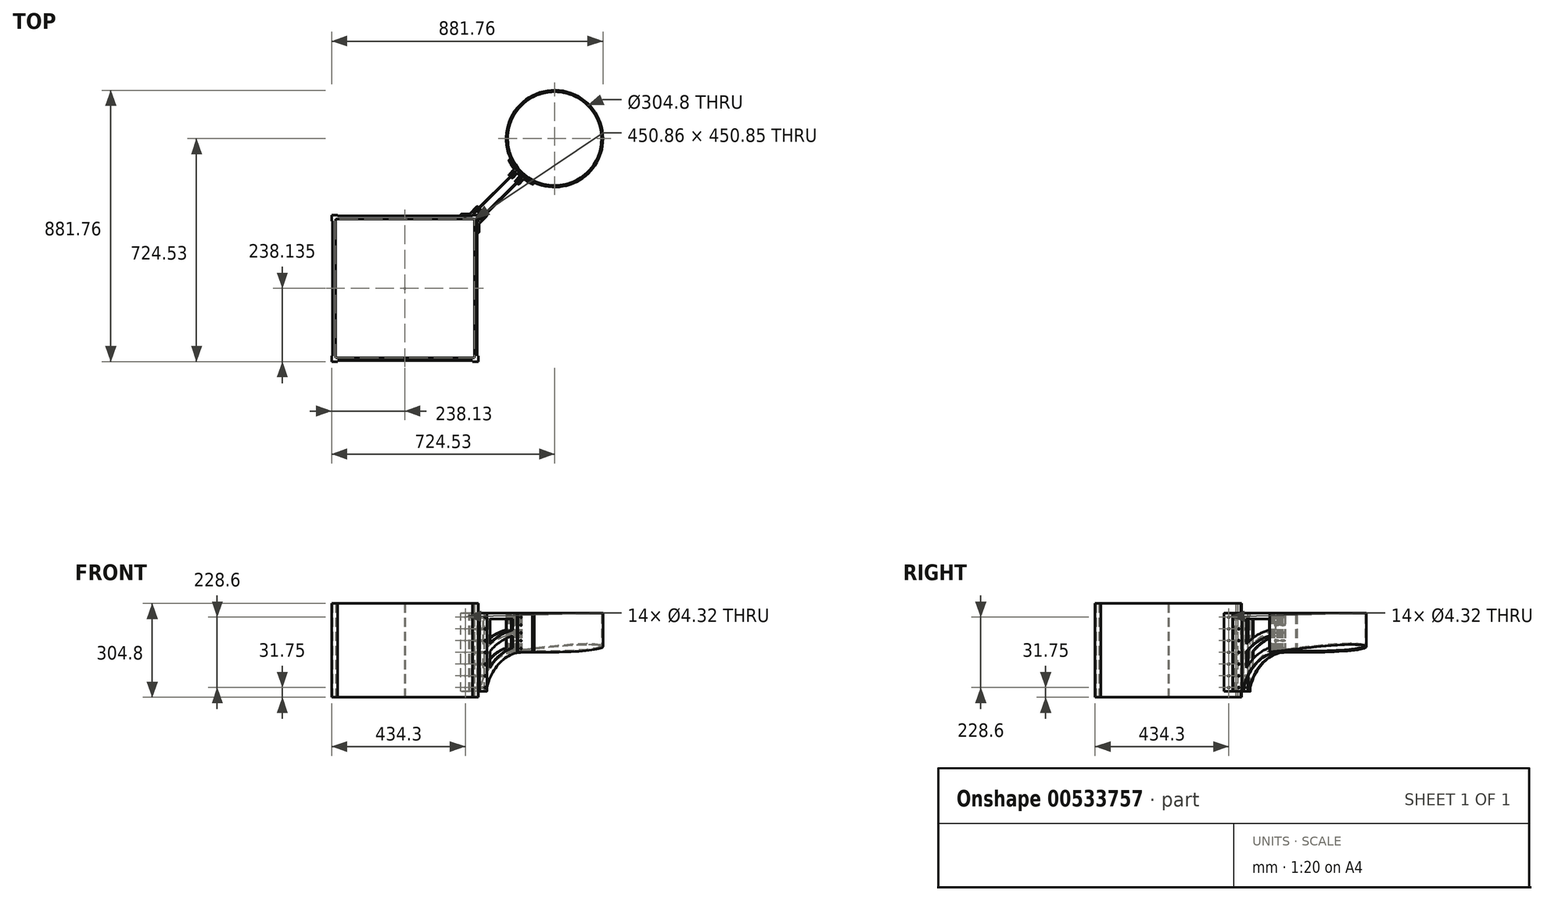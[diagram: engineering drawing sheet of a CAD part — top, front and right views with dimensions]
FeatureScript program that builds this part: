
annotation { "Feature Type Name" : "Feature", "Feature Type Description" : "" }
export const myFeature = defineFeature(function(context is Context, id is Id, definition is map)
    precondition{}
    {
        {
            var Q0;
            Q0=qCreatedBy(makeId("Top.planeOp"),FACE);
            var sketch = newSketch(context, id + "F0", { "sketchPlane" : qUnion([Q0])});
            skLineSegment(sketch, "E0.bottom", {"start": v(234.95, -234.95) * mm, "end": v(-234.95, -234.95) * mm});
            skLineSegment(sketch, "E0.top", {"start": v(234.95, 234.95) * mm, "end": v(-234.95, 234.95) * mm});
            skLineSegment(sketch, "E0.left", {"start": v(234.95, -234.95) * mm, "end": v(234.95, 234.95) * mm});
            skLineSegment(sketch, "E0.right", {"start": v(-234.95, -234.95) * mm, "end": v(-234.95, 234.95) * mm});
            skPoint(sketch, "E0.middle", {"position": v(0, 0) * mm});
            skLineSegment(sketch, "E1", {"start": v(0, 0) * mm, "end": v(234.95, 234.95) * mm});
            skLineSegment(sketch, "E2", {"start": v(234.95, 234.95) * mm, "end": v(486.4, 486.4) * mm});
            skCircle(sketch, "E3", {"center": v(486.4, 486.4) * mm, "radius": 152.4 * mm});
            skCircle(sketch, "E4", {"center": v(486.4, 486.4) * mm, "radius": 157.23 * mm});
            skLineSegment(sketch, "E5", {"start": v(-234.95, 234.95) * mm, "end": v(-234.95, 238.13) * mm});
            skLineSegment(sketch, "E6", {"start": v(-234.95, 238.13) * mm, "end": v(-238.13, 238.13) * mm});
            skLineSegment(sketch, "E7", {"start": v(-238.13, 238.13) * mm, "end": v(-238.13, 219.08) * mm});
            skLineSegment(sketch, "E8", {"start": v(-238.13, 219.08) * mm, "end": v(-234.95, 219.08) * mm});
            skLineSegment(sketch, "E9", {"start": v(-238.13, 238.13) * mm, "end": v(-219.08, 238.13) * mm});
            skLineSegment(sketch, "E10", {"start": v(-219.08, 238.13) * mm, "end": v(-219.08, 234.95) * mm});
            skLineSegment(sketch, "E11.1.0", {"start": v(-238.13, -238.13) * mm, "end": v(-219.08, -238.13) * mm});
            skLineSegment(sketch, "E11.1.1", {"start": v(-238.13, -238.13) * mm, "end": v(-238.13, -219.08) * mm});
            skLineSegment(sketch, "E11.1.2", {"start": v(-238.13, -219.08) * mm, "end": v(-234.95, -219.08) * mm});
            skLineSegment(sketch, "E11.1.3", {"start": v(-219.08, -238.13) * mm, "end": v(-219.08, -234.95) * mm});
            skLineSegment(sketch, "E11.1.4", {"start": v(-238.13, -234.95) * mm, "end": v(-238.13, -238.13) * mm});
            skLineSegment(sketch, "E11.1.5", {"start": v(-234.95, -234.95) * mm, "end": v(-238.13, -234.95) * mm});
            skLineSegment(sketch, "E11.2.0", {"start": v(238.13, -238.13) * mm, "end": v(238.13, -219.08) * mm});
            skLineSegment(sketch, "E11.2.1", {"start": v(238.13, -238.13) * mm, "end": v(219.08, -238.13) * mm});
            skLineSegment(sketch, "E11.2.2", {"start": v(219.08, -238.13) * mm, "end": v(219.08, -234.95) * mm});
            skLineSegment(sketch, "E11.2.3", {"start": v(238.13, -219.08) * mm, "end": v(234.95, -219.08) * mm});
            skLineSegment(sketch, "E11.2.4", {"start": v(234.95, -238.13) * mm, "end": v(238.13, -238.13) * mm});
            skLineSegment(sketch, "E11.2.5", {"start": v(234.95, -234.95) * mm, "end": v(234.95, -238.13) * mm});
            skLineSegment(sketch, "E11.3.0", {"start": v(238.13, 238.13) * mm, "end": v(219.08, 238.13) * mm});
            skLineSegment(sketch, "E11.3.1", {"start": v(238.13, 238.13) * mm, "end": v(238.13, 219.08) * mm});
            skLineSegment(sketch, "E11.3.2", {"start": v(238.13, 219.08) * mm, "end": v(234.95, 219.08) * mm});
            skLineSegment(sketch, "E11.3.3", {"start": v(219.08, 238.13) * mm, "end": v(219.08, 234.95) * mm});
            skLineSegment(sketch, "E11.3.4", {"start": v(238.13, 234.95) * mm, "end": v(238.13, 238.13) * mm});
            skLineSegment(sketch, "E11.3.5", {"start": v(234.95, 234.95) * mm, "end": v(238.13, 234.95) * mm});
            skLineSegment(sketch, "E12.0", {"start": v(-225.42, -225.42) * mm, "end": v(-225.43, 225.43) * mm});
            skLineSegment(sketch, "E12.1", {"start": v(225.43, -225.42) * mm, "end": v(-225.42, -225.42) * mm});
            skLineSegment(sketch, "E12.2", {"start": v(225.43, -225.42) * mm, "end": v(225.42, 225.43) * mm});
            skLineSegment(sketch, "E12.3", {"start": v(225.42, 225.43) * mm, "end": v(-225.43, 225.43) * mm});
            skSolve(sketch);
        }
        {
            var Q0;
            Q0=makeQuery(id+"F0.imprint","IMPRINT",FACE,{"disambiguationData":[TD([[makeQuery(id+"F0.imprint","IMPRINT",EDGE,{"derivedFrom":sQuery(id+"F0.wireOp",EDGE,"E3")}),-1.0]])]});
            extrude(context, id + "F1", {"entities" : qUnion([Q0]), "depth" : 304.8 * mm, "offsetDistance" : 25.4 * mm});
        }
        {
            var Q0;
            Q0=makeQuery(id+"F0.imprint","IMPRINT",FACE,{"disambiguationData":[TD([[makeQuery(id+"F0.imprint","IMPRINT",EDGE,{"derivedFrom":sQuery(id+"F0.wireOp",EDGE,"E12.0")}),1.0]])]});
            var Q1;
            Q1=makeQuery(id+"F0.imprint","IMPRINT",FACE,{"disambiguationData":[TD([[makeQuery(id+"F0.imprint","IMPRINT",EDGE,{"derivedFrom":sQuery(id+"F0.wireOp",EDGE,"E11.3.1")}),-1.0]])]});
            var Q2;
            {var subQ4=sQuery(id+"F0.wireOp",EDGE,"E11.3.0");Q2=makeQuery(id+"F0.imprint","IMPRINT",FACE,{"disambiguationData":[TD([[makeQuery(id+"F0.imprint","IMPRINT",EDGE,{"derivedFrom":subQ4}),1.0]])]});}
            var Q3;
            Q3=makeQuery(id+"F0.imprint","IMPRINT",FACE,{"disambiguationData":[TD([[makeQuery(id+"F0.imprint","IMPRINT",EDGE,{"derivedFrom":sQuery(id+"F0.wireOp",EDGE,"E11.2.0")}),1.0]])]});
            var Q4;
            {var subQ1=sQuery(id+"F0.wireOp",EDGE,"E5");Q4=makeQuery(id+"F0.imprint","IMPRINT",FACE,{"disambiguationData":[TD([[makeQuery(id+"F0.imprint","IMPRINT",EDGE,{"derivedFrom":subQ1}),1.0]])]});}
            var Q5;
            Q5=makeQuery(id+"F0.imprint","IMPRINT",FACE,{"disambiguationData":[TD([[makeQuery(id+"F0.imprint","IMPRINT",EDGE,{"derivedFrom":sQuery(id+"F0.wireOp",EDGE,"E11.2.1")}),-1.0]])]});
            var Q6;
            {var subQ0=sQuery(id+"F0.wireOp",EDGE,"E5");Q6=makeQuery(id+"F0.imprint","IMPRINT",FACE,{"disambiguationData":[TD([[makeQuery(id+"F0.imprint","IMPRINT",EDGE,{"derivedFrom":subQ0}),-1.0]])]});}
            var Q7;
            Q7=makeQuery(id+"F0.imprint","IMPRINT",FACE,{"disambiguationData":[TD([[makeQuery(id+"F0.imprint","IMPRINT",EDGE,{"derivedFrom":sQuery(id+"F0.wireOp",EDGE,"E11.1.0")}),1.0]])]});
            var Q8;
            Q8=makeQuery(id+"F0.imprint","IMPRINT",FACE,{"disambiguationData":[TD([[makeQuery(id+"F0.imprint","IMPRINT",EDGE,{"derivedFrom":sQuery(id+"F0.wireOp",EDGE,"E11.1.1")}),-1.0]])]});
            var Q9;
            {var subQ2=sQuery(id+"F0.wireOp",EDGE,"E11.3.4");Q9=makeQuery(id+"F0.imprint","IMPRINT",FACE,{"disambiguationData":[TD([[makeQuery(id+"F0.imprint","IMPRINT",EDGE,{"derivedFrom":subQ2}),1.0]])]});}
            extrude(context, id + "F2", {"entities" : qUnion([Q0, Q1, Q2, Q3, Q4, Q5, Q6, Q7, Q8, Q9]), "depth" : 304.8 * mm, "offsetDistance" : 25.4 * mm});
        }
        {
            var Q0;
            Q0=makeQuery(id+"F1.opExtrude","CAP_FACE",FACE,{"disambiguationData":[OSD([sQuery(id+"F0.wireOp",EDGE,"E3"),sQuery(id+"F0.wireOp",EDGE,"E4")])],"isStart":false});
            var sketch = newSketch(context, id + "F3", { "sketchPlane" : qUnion([Q0])});
            skCircle(sketch, "E13", {"center": v(486.4, 486.4) * mm, "radius": 157.23 * mm});
            skArc(sketch, "E14", {"start": v(366.99, 372.3) * mm, "mid": v(369.6, 369.6) * mm, "end": v(372.3, 366.99) * mm});
            skLineSegment(sketch, "E15", {"start": v(486.4, 486.4) * mm, "end": v(643.62, 486.4) * mm});
            skLineSegment(sketch, "E16", {"start": v(643.62, 486.4) * mm, "end": v(645.21, 486.4) * mm});
            skCircle(sketch, "E17", {"center": v(486.4, 486.4) * mm, "radius": 158.81 * mm});
            skLineSegment(sketch, "E18", {"start": v(369.6, 369.6) * mm, "end": v(244.47, 244.48) * mm});
            skLineSegment(sketch, "E19", {"start": v(486.4, 486.4) * mm, "end": v(477.42, 495.38) * mm});
            skLineSegment(sketch, "E20", {"start": v(360.97, 378.93) * mm, "end": v(345.53, 363.49) * mm});
            skLineSegment(sketch, "E21", {"start": v(477.42, 495.38) * mm, "end": v(475.17, 497.62) * mm});
            skLineSegment(sketch, "E22", {"start": v(358.92, 381.37) * mm, "end": v(343.28, 365.73) * mm});
            skLineSegment(sketch, "E23", {"start": v(645.21, 486.4) * mm, "end": v(651.56, 486.4) * mm});
            skLineSegment(sketch, "E24", {"start": v(238.13, 238.13) * mm, "end": v(219.08, 238.13) * mm});
            skLineSegment(sketch, "E25", {"start": v(219.08, 238.13) * mm, "end": v(219.08, 234.95) * mm});
            skLineSegment(sketch, "E26", {"start": v(219.08, 234.95) * mm, "end": v(180.98, 234.95) * mm});
            skLineSegment(sketch, "E27", {"start": v(180.98, 234.95) * mm, "end": v(180.98, 238.76) * mm});
            skLineSegment(sketch, "E28", {"start": v(475.17, 497.62) * mm, "end": v(470.68, 502.11) * mm});
            skLineSegment(sketch, "E29", {"start": v(353.4, 384.83) * mm, "end": v(338.8, 370.22) * mm});
            skLineSegment(sketch, "E30", {"start": v(477.42, 495.38) * mm, "end": v(481.9, 490.89) * mm});
            skLineSegment(sketch, "E31", {"start": v(363.35, 372.33) * mm, "end": v(350.02, 359) * mm});
            skLineSegment(sketch, "E32", {"start": v(353.4, 384.83) * mm, "end": v(337, 368.43) * mm});
            skLineSegment(sketch, "E33", {"start": v(338.8, 366.63) * mm, "end": v(339.69, 365.73) * mm});
            skArc(sketch, "E34.trimOffspring", {"start": v(358.92, 381.37) * mm, "mid": v(359.94, 380.15) * mm, "end": v(360.97, 378.93) * mm});
            skLineSegment(sketch, "E35.trimOffspring", {"start": v(345.53, 359.9) * mm, "end": v(346.42, 359) * mm});
            skLineSegment(sketch, "E36", {"start": v(235.5, 244.48) * mm, "end": v(245.3, 254.29) * mm});
            skLineSegment(sketch, "E37", {"start": v(245.3, 257.88) * mm, "end": v(244.41, 258.78) * mm});
            skLineSegment(sketch, "E38.trimOffspring", {"start": v(234.08, 265.51) * mm, "end": v(210.61, 242.04) * mm});
            skLineSegment(sketch, "E39.trimOffspring", {"start": v(247.1, 256.09) * mm, "end": v(235.5, 244.47) * mm});
            skLineSegment(sketch, "E40", {"start": v(183.52, 241.3) * mm, "end": v(208.82, 241.3) * mm});
            skLineSegment(sketch, "E41", {"start": v(238.13, 244.48) * mm, "end": v(235.5, 244.48) * mm});
            skLineSegment(sketch, "E42", {"start": v(223.34, 241.3) * mm, "end": v(221.1, 243.55) * mm});
            skLineSegment(sketch, "E43.trimOffspring", {"start": v(238.57, 264.62) * mm, "end": v(237.68, 265.51) * mm});
            skLineSegment(sketch, "E44", {"start": v(486.4, 486.4) * mm, "end": v(339.03, 417.68) * mm});
            skPoint(sketch, "E45.visualSharp", {"position": v(354.96, 386.39) * mm});
            skArc(sketch, "E45.filletArc", {"start": v(353.4, 384.83) * mm, "mid": v(354.13, 386.44) * mm, "end": v(353.64, 388.14) * mm});
            skPoint(sketch, "E46.visualSharp", {"position": v(337, 368.43) * mm});
            skArc(sketch, "E46.filletArc", {"start": v(338.8, 370.22) * mm, "mid": v(338.05, 368.43) * mm, "end": v(338.8, 366.63) * mm});
            skPoint(sketch, "E47.visualSharp", {"position": v(348.22, 357.2) * mm});
            skArc(sketch, "E47.filletArc", {"start": v(346.42, 359) * mm, "mid": v(348.22, 358.25) * mm, "end": v(350.02, 359) * mm});
            skPoint(sketch, "E48.visualSharp", {"position": v(365.2, 374.19) * mm});
            skArc(sketch, "E48.filletArc", {"start": v(366.99, 372.3) * mm, "mid": v(365.18, 373.08) * mm, "end": v(363.35, 372.33) * mm});
            skPoint(sketch, "E49.visualSharp", {"position": v(235.88, 267.31) * mm});
            skArc(sketch, "E49.filletArc", {"start": v(237.68, 265.51) * mm, "mid": v(235.88, 266.26) * mm, "end": v(234.08, 265.51) * mm});
            skPoint(sketch, "E50.visualSharp", {"position": v(247.1, 256.09) * mm});
            skArc(sketch, "E50.filletArc", {"start": v(245.3, 254.29) * mm, "mid": v(246.05, 256.09) * mm, "end": v(245.3, 257.88) * mm});
            skPoint(sketch, "E51.visualSharp", {"position": v(209.87, 241.3) * mm});
            skArc(sketch, "E51.filletArc", {"start": v(208.82, 241.3) * mm, "mid": v(209.79, 241.5) * mm, "end": v(210.61, 242.04) * mm});
            skPoint(sketch, "E52.visualSharp", {"position": v(180.98, 241.3) * mm});
            skArc(sketch, "E52.filletArc", {"start": v(183.52, 241.3) * mm, "mid": v(181.72, 240.56) * mm, "end": v(180.98, 238.76) * mm});
            skLineSegment(sketch, "E53.trimOffspring", {"start": v(238.57, 261.02) * mm, "end": v(221.1, 243.55) * mm});
            skLineSegment(sketch, "E54.trimOffspring", {"start": v(240.82, 258.78) * mm, "end": v(223.34, 241.3) * mm});
            skPoint(sketch, "E55.visualSharp", {"position": v(341.49, 363.94) * mm});
            skArc(sketch, "E55.filletArc", {"start": v(339.69, 365.73) * mm, "mid": v(341.49, 364.99) * mm, "end": v(343.28, 365.73) * mm});
            skPoint(sketch, "E56.visualSharp", {"position": v(343.73, 361.7) * mm});
            skArc(sketch, "E56.filletArc", {"start": v(345.53, 363.49) * mm, "mid": v(344.78, 361.7) * mm, "end": v(345.53, 359.9) * mm});
            skPoint(sketch, "E57.visualSharp", {"position": v(240.37, 262.82) * mm});
            skArc(sketch, "E57.filletArc", {"start": v(238.57, 261.02) * mm, "mid": v(239.32, 262.82) * mm, "end": v(238.57, 264.62) * mm});
            skPoint(sketch, "E58.visualSharp", {"position": v(242.62, 260.58) * mm});
            skArc(sketch, "E58.filletArc", {"start": v(244.41, 258.78) * mm, "mid": v(242.62, 259.52) * mm, "end": v(240.82, 258.78) * mm});
            skLineSegment(sketch, "E59.MirrorCS", {"start": v(359.9, 345.53) * mm, "end": v(359, 346.42) * mm});
            skArc(sketch, "E60.MirrorCS", {"start": v(363.49, 345.53) * mm, "mid": v(361.7, 344.78) * mm, "end": v(359.9, 345.53) * mm});
            skLineSegment(sketch, "E61.MirrorCS", {"start": v(366.63, 338.8) * mm, "end": v(365.73, 339.69) * mm});
            skArc(sketch, "E62.MirrorCS", {"start": v(372.3, 366.99) * mm, "mid": v(373.08, 365.18) * mm, "end": v(372.33, 363.35) * mm});
            skArc(sketch, "E63.MirrorCS", {"start": v(384.83, 353.4) * mm, "mid": v(386.44, 354.13) * mm, "end": v(388.14, 353.64) * mm});
            skArc(sketch, "E64.MirrorCS", {"start": v(359, 346.42) * mm, "mid": v(358.25, 348.22) * mm, "end": v(359, 350.02) * mm});
            skArc(sketch, "E65.MirrorCS", {"start": v(365.73, 339.69) * mm, "mid": v(364.99, 341.49) * mm, "end": v(365.73, 343.28) * mm});
            skArc(sketch, "E66.MirrorCS", {"start": v(370.22, 338.8) * mm, "mid": v(368.43, 338.05) * mm, "end": v(366.63, 338.8) * mm});
            skArc(sketch, "E67.MirrorCS", {"start": v(381.37, 358.92) * mm, "mid": v(380.15, 359.94) * mm, "end": v(378.93, 360.97) * mm});
            skLineSegment(sketch, "E68.MirrorCS", {"start": v(384.83, 353.4) * mm, "end": v(368.43, 337) * mm});
            skPoint(sketch, "E69.MirrorP", {"position": v(386.39, 354.96) * mm});
            skPoint(sketch, "E70.MirrorP", {"position": v(363.94, 341.49) * mm});
            skPoint(sketch, "E71.MirrorP", {"position": v(368.43, 337) * mm});
            skPoint(sketch, "E72.MirrorP", {"position": v(361.7, 343.73) * mm});
            skPoint(sketch, "E73.MirrorP", {"position": v(374.19, 365.2) * mm});
            skPoint(sketch, "E74.MirrorP", {"position": v(357.2, 348.22) * mm});
            skLineSegment(sketch, "E75.MirrorCS", {"start": v(381.37, 358.92) * mm, "end": v(365.73, 343.28) * mm});
            skLineSegment(sketch, "E76.MirrorCS", {"start": v(372.33, 363.35) * mm, "end": v(359, 350.02) * mm});
            skLineSegment(sketch, "E77.MirrorCS", {"start": v(378.93, 360.97) * mm, "end": v(363.49, 345.53) * mm});
            skLineSegment(sketch, "E78.MirrorCS", {"start": v(384.83, 353.4) * mm, "end": v(370.22, 338.8) * mm});
            skLineSegment(sketch, "E79.MirrorCS", {"start": v(486.4, 486.4) * mm, "end": v(417.68, 339.03) * mm});
            skLineSegment(sketch, "E80.MirrorCS", {"start": v(238.13, 219.08) * mm, "end": v(234.95, 219.08) * mm});
            skArc(sketch, "E81.MirrorCS", {"start": v(258.78, 244.41) * mm, "mid": v(259.52, 242.62) * mm, "end": v(258.78, 240.82) * mm});
            skArc(sketch, "E82.MirrorCS", {"start": v(265.51, 237.68) * mm, "mid": v(266.26, 235.88) * mm, "end": v(265.51, 234.08) * mm});
            skArc(sketch, "E83.MirrorCS", {"start": v(254.29, 245.3) * mm, "mid": v(256.09, 246.05) * mm, "end": v(257.88, 245.3) * mm});
            skLineSegment(sketch, "E84.MirrorCS", {"start": v(264.62, 238.57) * mm, "end": v(265.51, 237.68) * mm});
            skArc(sketch, "E85.MirrorCS", {"start": v(241.3, 208.82) * mm, "mid": v(241.5, 209.79) * mm, "end": v(242.04, 210.61) * mm});
            skLineSegment(sketch, "E86.MirrorCS", {"start": v(244.47, 238.13) * mm, "end": v(244.47, 235.5) * mm});
            skArc(sketch, "E87.MirrorCS", {"start": v(261.02, 238.57) * mm, "mid": v(262.82, 239.32) * mm, "end": v(264.62, 238.57) * mm});
            skArc(sketch, "E88.MirrorCS", {"start": v(241.3, 183.52) * mm, "mid": v(240.56, 181.72) * mm, "end": v(238.76, 180.98) * mm});
            skLineSegment(sketch, "E89.MirrorCS", {"start": v(257.88, 245.3) * mm, "end": v(258.78, 244.41) * mm});
            skLineSegment(sketch, "E90.MirrorCS", {"start": v(241.3, 223.34) * mm, "end": v(243.55, 221.1) * mm});
            skLineSegment(sketch, "E91.MirrorCS", {"start": v(234.95, 180.98) * mm, "end": v(238.76, 180.98) * mm});
            skLineSegment(sketch, "E92.MirrorCS", {"start": v(244.47, 235.5) * mm, "end": v(254.29, 245.3) * mm});
            skLineSegment(sketch, "E93.MirrorCS", {"start": v(238.13, 238.13) * mm, "end": v(238.13, 219.08) * mm});
            skPoint(sketch, "E94.MirrorP", {"position": v(256.09, 247.1) * mm});
            skPoint(sketch, "E95.MirrorP", {"position": v(262.82, 240.37) * mm});
            skPoint(sketch, "E96.MirrorP", {"position": v(241.3, 209.87) * mm});
            skLineSegment(sketch, "E97.MirrorCS", {"start": v(265.51, 234.08) * mm, "end": v(242.04, 210.61) * mm});
            skPoint(sketch, "E98.MirrorP", {"position": v(260.58, 242.62) * mm});
            skLineSegment(sketch, "E99.MirrorCS", {"start": v(261.02, 238.57) * mm, "end": v(243.55, 221.1) * mm});
            skPoint(sketch, "E100.MirrorP", {"position": v(267.31, 235.88) * mm});
            skLineSegment(sketch, "E101.MirrorCS", {"start": v(258.78, 240.82) * mm, "end": v(241.3, 223.34) * mm});
            skPoint(sketch, "E102.MirrorP", {"position": v(241.3, 180.98) * mm});
            skLineSegment(sketch, "E103.MirrorCS", {"start": v(241.3, 183.52) * mm, "end": v(241.3, 208.82) * mm});
            skLineSegment(sketch, "E104.MirrorCS", {"start": v(256.09, 247.1) * mm, "end": v(244.47, 235.5) * mm});
            skLineSegment(sketch, "E105.MirrorCS", {"start": v(234.95, 219.08) * mm, "end": v(234.95, 180.98) * mm});
            skLineSegment(sketch, "E106", {"start": v(238.13, 244.48) * mm, "end": v(241.94, 244.48) * mm});
            skLineSegment(sketch, "E107", {"start": v(244.47, 241.94) * mm, "end": v(244.47, 238.13) * mm});
            skPoint(sketch, "E108.MirrorCS.start.orphan", {"position": v(238.12, 238.13) * mm});
            skPoint(sketch, "E109.visualSharp", {"position": v(244.47, 244.48) * mm});
            skArc(sketch, "E109.filletArc", {"start": v(244.47, 241.94) * mm, "mid": v(243.73, 243.73) * mm, "end": v(241.94, 244.48) * mm});
            skLineSegment(sketch, "E110.0", {"start": v(216.54, 238.13) * mm, "end": v(216.54, 234.95) * mm});
            skLineSegment(sketch, "E111.0", {"start": v(238.13, 216.53) * mm, "end": v(234.95, 216.53) * mm});
            skLineSegment(sketch, "E112", {"start": v(219.08, 238.13) * mm, "end": v(216.54, 238.13) * mm});
            skLineSegment(sketch, "E113", {"start": v(238.13, 216.53) * mm, "end": v(238.13, 219.08) * mm});
            skArc(sketch, "E114.trimOffspring", {"start": v(378.93, 360.97) * mm, "mid": v(380.15, 359.94) * mm, "end": v(381.37, 358.92) * mm});
            skArc(sketch, "E115.trimOffspring", {"start": v(388.14, 353.64) * mm, "mid": v(400.83, 345.12) * mm, "end": v(414.27, 337.82) * mm});
            skArc(sketch, "E116.trimOffspring", {"start": v(337.82, 414.27) * mm, "mid": v(345.12, 400.83) * mm, "end": v(353.64, 388.14) * mm});
            skPoint(sketch, "E117.visualSharp", {"position": v(336.7, 416.6) * mm});
            skArc(sketch, "E117.filletArc", {"start": v(339.03, 417.68) * mm, "mid": v(337.7, 416.23) * mm, "end": v(337.82, 414.27) * mm});
            skPoint(sketch, "E118.visualSharp", {"position": v(416.6, 336.7) * mm});
            skArc(sketch, "E118.filletArc", {"start": v(414.27, 337.82) * mm, "mid": v(416.23, 337.7) * mm, "end": v(417.68, 339.03) * mm});
            skSolve(sketch);
        }
        {
            var Q0;
            Q0=makeQuery(id+"F3.imprint","IMPRINT",FACE,{"disambiguationData":[TD([[makeQuery(id+"F3.imprint","IMPRINT",EDGE,{"derivedFrom":sQuery(id+"F3.wireOp",EDGE,"E20")}),1.0]])]});
            var Q1;
            Q1=makeQuery(id+"F3.imprint","IMPRINT",FACE,{"disambiguationData":[TD([[makeQuery(id+"F3.imprint","IMPRINT",EDGE,{"derivedFrom":sQuery(id+"F3.wireOp",EDGE,"E24")}),-1.0]])]});
            extrude(context, id + "F4", {"entities" : qUnion([Q0, Q1]), "oppositeDirection" : true, "depth" : 254 * mm, "offsetDistance" : 25.4 * mm});
        }
        {
            var Q0;
            Q0=makeQuery(id+"F4.opExtrude","SWEPT_FACE",FACE,{"disambiguationData":[OSD([sQuery(id+"F3.wireOp",EDGE,"E97.MirrorCS")])]});
            var sketch = newSketch(context, id + "F5", { "sketchPlane" : qUnion([Q0])});
            skLineSegment(sketch, "E119", {"start": v(538.63, 304.8) * mm, "end": v(538.63, 177.8) * mm});
            skLineSegment(sketch, "E120", {"start": v(538.63, 177.8) * mm, "end": v(487.83, 177.8) * mm});
            skLineSegment(sketch, "E121", {"start": v(487.83, 177.8) * mm, "end": v(487.83, -25.4) * mm});
            skLineSegment(sketch, "E122", {"start": v(487.83, -25.4) * mm, "end": v(564.03, -25.4) * mm});
            skLineSegment(sketch, "E123", {"start": v(564.03, -25.4) * mm, "end": v(564.03, 177.8) * mm});
            skLineSegment(sketch, "E124", {"start": v(564.03, 177.8) * mm, "end": v(538.63, 177.8) * mm});
            skSolve(sketch);
        }
        {
            var Q0;
            Q0=makeQuery(id+"F5.imprint","IMPRINT",FACE,{"disambiguationData":[TD([[makeQuery(id+"F5.imprint","IMPRINT",EDGE,{"derivedFrom":sQuery(id+"F5.wireOp",EDGE,"E120")}),1.0]])]});
            extrude(context, id + "F6", {"entities" : qUnion([Q0]), "operationType" : NewBodyOperationType.REMOVE, "endBound" : BoundingType.SYMMETRIC, "oppositeDirection" : true, "depth" : 254 * mm, "offsetDistance" : 25.4 * mm});
        }
        {
            var Q0;
            Q0=makeQuery(id+"F4.opExtrude","SWEPT_FACE",FACE,{"disambiguationData":[OSD([sQuery(id+"F3.wireOp",EDGE,"E42")])]});
            var Q1;
            Q1=makeQuery(id+"F4.opExtrude","SWEPT_FACE",FACE,{"disambiguationData":[OSD([sQuery(id+"F3.wireOp",EDGE,"E90.MirrorCS")])]});
            extrude(context, id + "F7", {"entities" : qUnion([Q0, Q1]), "depth" : 194.3 * mm, "offsetDistance" : 25.4 * mm});
        }
        {
            var Q0;
            Q0=makeQuery(id+"F7.opExtrude","SWEPT_FACE",FACE,{"disambiguationData":[OSD([sQuery(id+"F3.wireOp",EDGE,"E90.MirrorCS"),sQuery(id+"F3.wireOp",EDGE,"E99.MirrorCS")])]});
            var sketch = newSketch(context, id + "F8", { "sketchPlane" : qUnion([Q0])});
            skLineSegment(sketch, "E125", {"start": v(355.8, 50.8) * mm, "end": v(355.8, 37.36) * mm});
            skLineSegment(sketch, "E126", {"start": v(522.86, 177.8) * mm, "end": v(532.9, 177.8) * mm});
            skArc(sketch, "E127", {"start": v(522.86, 177.8) * mm, "mid": v(417.94, 142.44) * mm, "end": v(355.8, 50.8) * mm});
            skLineSegment(sketch, "E128", {"start": v(355.8, 37.36) * mm, "end": v(550.78, 37.36) * mm});
            skLineSegment(sketch, "E129", {"start": v(532.9, 177.8) * mm, "end": v(532.9, 37.36) * mm});
            skSolve(sketch);
        }
        {
            var Q0;
            Q0 = qSketchRegion(id + "F8", true);
            extrude(context, id + "F9", {"entities" : qUnion([Q0]), "operationType" : NewBodyOperationType.REMOVE, "oppositeDirection" : true, "depth" : 127 * mm, "offsetDistance" : 25.4 * mm});
        }
        {
            var Q0;
            {var subQ0=sQuery(id+"F3.wireOp",EDGE,"E44");var subQ1=sQuery(id+"F3.wireOp",EDGE,"E13");var subQ2=makeQuery(id+"F3.imprint","INTERSECT",VERTEX,{"derivedFrom":[subQ1,subQ0]});Q0=makeQuery(id+"F3.imprint","IMPRINT",FACE,{"disambiguationData":[TD([[makeQuery(id+"F3.imprint","IMPRINT",EDGE,{"disambiguationData":[TD([[subQ2,-1.0]])],"derivedFrom":subQ1}),-1.0]])]});}
            extrude(context, id + "F10", {"entities" : qUnion([Q0]), "oppositeDirection" : true, "depth" : 127 * mm, "offsetDistance" : 25.4 * mm});
        }
        {
            var Q0;
            Q0=sQuery(id+"F3.wireOp",EDGE,"E18");
            cPlane(context, id + "F11", {"entities" : qUnion([Q0]), "cplaneType" : CPlaneType.LINE_ANGLE, "offset" : 25.4 * mm, "angle" : 90 * degree, "width" : 152.4 * mm, "height" : 152.4 * mm});
        }
        {
            var Q0;
            Q0=qCreatedBy(id+"F11.planeOp",FACE);
            var sketch = newSketch(context, id + "F12", { "sketchPlane" : qUnion([Q0])});
            skLineSegment(sketch, "E130", {"start": v(521.3, 304.8) * mm, "end": v(521.3, 275.68) * mm});
            skLineSegment(sketch, "E131", {"start": v(521.3, 304.8) * mm, "end": v(687.87, 304.8) * mm});
            skLineSegment(sketch, "E132", {"start": v(687.87, 304.8) * mm, "end": v(530.64, 304.8) * mm});
            skLineSegment(sketch, "E133", {"start": v(530.64, 304.8) * mm, "end": v(530.64, 177.8) * mm});
            skLineSegment(sketch, "E134", {"start": v(687.87, 304.8) * mm, "end": v(845.1, 304.8) * mm});
            skLineSegment(sketch, "E135", {"start": v(845.1, 304.8) * mm, "end": v(845.1, 203.2) * mm});
            skLineSegment(sketch, "E136", {"start": v(530.64, 177.8) * mm, "end": v(526.36, 177.8) * mm});
            skArc(sketch, "E137", {"start": v(530.64, 177.8) * mm, "mid": v(688.38, 184.16) * mm, "end": v(845.1, 203.2) * mm});
            skLineSegment(sketch, "E138", {"start": v(845.1, 203.2) * mm, "end": v(870.5, 203.2) * mm});
            skLineSegment(sketch, "E139", {"start": v(870.5, 203.2) * mm, "end": v(870.5, -50.8) * mm});
            skLineSegment(sketch, "E140", {"start": v(870.5, -50.8) * mm, "end": v(526.36, -50.8) * mm});
            skLineSegment(sketch, "E141", {"start": v(526.36, 177.8) * mm, "end": v(526.36, -50.8) * mm});
            skSolve(sketch);
        }
        {
            var Q0;
            Q0=makeQuery(id+"F12.imprint","IMPRINT",FACE,{"disambiguationData":[TD([[makeQuery(id+"F12.imprint","IMPRINT",EDGE,{"derivedFrom":sQuery(id+"F12.wireOp",EDGE,"E136")}),1.0]])]});
            extrude(context, id + "F13", {"entities" : qUnion([Q0]), "operationType" : NewBodyOperationType.REMOVE, "endBound" : BoundingType.SYMMETRIC, "oppositeDirection" : true, "depth" : 381 * mm, "offsetDistance" : 25.4 * mm});
        }
        {
            var Q0;
            Q0=qCreatedBy(makeId("Top.planeOp"),FACE);
            var sketch = newSketch(context, id + "F14", { "sketchPlane" : qUnion([Q0])});
            skCircle(sketch, "E142", {"center": v(0, 0) * mm, "radius": 1.27 * mm});
            skSolve(sketch);
        }
        {
            var Q0;
            Q0 = qSketchRegion(id + "F14", true);
            extrude(context, id + "F15", {"entities" : qUnion([Q0]), "depth" : 304.8 * mm, "offsetDistance" : 25.4 * mm});
        }
        {
            var Q0;
            Q0=makeQuery(id+"F1.opExtrude","SWEPT_FACE",FACE,{"disambiguationData":[OSD([sQuery(id+"F0.wireOp",EDGE,"E3")])]});
            fillet(context, id + "F16", {"entities" : qUnion([Q0]), "radius" : 3.8 * mm, "tangentPropagation" : true, "allowEdgeOverflow" : false});
        }
        {
            var Q0;
            Q0=makeQuery(id+"F1.opExtrude","SWEPT_BODY",BODY,{"disambiguationData":[OSD([sQuery(id+"F0.wireOp",EDGE,"E3"),sQuery(id+"F0.wireOp",EDGE,"E4")])]});
            var Q1;
            Q1=makeQuery(id+"F4.opExtrude","SWEPT_BODY",BODY,{"disambiguationData":[OSD([sQuery(id+"F3.wireOp",EDGE,"E14"),sQuery(id+"F3.wireOp",EDGE,"E17"),sQuery(id+"F3.wireOp",EDGE,"E20"),sQuery(id+"F3.wireOp",EDGE,"E22"),sQuery(id+"F3.wireOp",EDGE,"E31"),sQuery(id+"F3.wireOp",EDGE,"E32"),sQuery(id+"F3.wireOp",EDGE,"E33"),sQuery(id+"F3.wireOp",EDGE,"E34.trimOffspring"),sQuery(id+"F3.wireOp",EDGE,"E35.trimOffspring"),sQuery(id+"F3.wireOp",EDGE,"E44"),sQuery(id+"F3.wireOp",EDGE,"E45.filletArc"),sQuery(id+"F3.wireOp",EDGE,"E46.filletArc"),sQuery(id+"F3.wireOp",EDGE,"E47.filletArc"),sQuery(id+"F3.wireOp",EDGE,"E48.filletArc"),sQuery(id+"F3.wireOp",EDGE,"E55.filletArc"),sQuery(id+"F3.wireOp",EDGE,"E56.filletArc"),sQuery(id+"F3.wireOp",EDGE,"E59.MirrorCS"),sQuery(id+"F3.wireOp",EDGE,"E60.MirrorCS"),sQuery(id+"F3.wireOp",EDGE,"E61.MirrorCS"),sQuery(id+"F3.wireOp",EDGE,"E62.MirrorCS"),sQuery(id+"F3.wireOp",EDGE,"E63.MirrorCS"),sQuery(id+"F3.wireOp",EDGE,"E64.MirrorCS"),sQuery(id+"F3.wireOp",EDGE,"E65.MirrorCS"),sQuery(id+"F3.wireOp",EDGE,"E66.MirrorCS"),sQuery(id+"F3.wireOp",EDGE,"E75.MirrorCS"),sQuery(id+"F3.wireOp",EDGE,"E76.MirrorCS"),sQuery(id+"F3.wireOp",EDGE,"E77.MirrorCS"),sQuery(id+"F3.wireOp",EDGE,"E78.MirrorCS"),sQuery(id+"F3.wireOp",EDGE,"E79.MirrorCS"),sQuery(id+"F3.wireOp",EDGE,"E114.trimOffspring"),sQuery(id+"F3.wireOp",EDGE,"E115.trimOffspring"),sQuery(id+"F3.wireOp",EDGE,"E116.trimOffspring"),sQuery(id+"F3.wireOp",EDGE,"E117.filletArc"),sQuery(id+"F3.wireOp",EDGE,"E118.filletArc")])]});
            var Q2;
            Q2=makeQuery(id+"F4.opExtrude","SWEPT_BODY",BODY,{"disambiguationData":[OSD([sQuery(id+"F3.wireOp",EDGE,"E24"),sQuery(id+"F3.wireOp",EDGE,"E26"),sQuery(id+"F3.wireOp",EDGE,"E27"),sQuery(id+"F3.wireOp",EDGE,"E37"),sQuery(id+"F3.wireOp",EDGE,"E38.trimOffspring"),sQuery(id+"F3.wireOp",EDGE,"E39.trimOffspring"),sQuery(id+"F3.wireOp",EDGE,"E40"),sQuery(id+"F3.wireOp",EDGE,"E41"),sQuery(id+"F3.wireOp",EDGE,"E42"),sQuery(id+"F3.wireOp",EDGE,"E43.trimOffspring"),sQuery(id+"F3.wireOp",EDGE,"E49.filletArc"),sQuery(id+"F3.wireOp",EDGE,"E50.filletArc"),sQuery(id+"F3.wireOp",EDGE,"E51.filletArc"),sQuery(id+"F3.wireOp",EDGE,"E52.filletArc"),sQuery(id+"F3.wireOp",EDGE,"E53.trimOffspring"),sQuery(id+"F3.wireOp",EDGE,"E54.trimOffspring"),sQuery(id+"F3.wireOp",EDGE,"E57.filletArc"),sQuery(id+"F3.wireOp",EDGE,"E58.filletArc"),sQuery(id+"F3.wireOp",EDGE,"E81.MirrorCS"),sQuery(id+"F3.wireOp",EDGE,"E82.MirrorCS"),sQuery(id+"F3.wireOp",EDGE,"E83.MirrorCS"),sQuery(id+"F3.wireOp",EDGE,"E84.MirrorCS"),sQuery(id+"F3.wireOp",EDGE,"E85.MirrorCS"),sQuery(id+"F3.wireOp",EDGE,"E86.MirrorCS"),sQuery(id+"F3.wireOp",EDGE,"E87.MirrorCS"),sQuery(id+"F3.wireOp",EDGE,"E88.MirrorCS"),sQuery(id+"F3.wireOp",EDGE,"E89.MirrorCS"),sQuery(id+"F3.wireOp",EDGE,"E90.MirrorCS"),sQuery(id+"F3.wireOp",EDGE,"E91.MirrorCS"),sQuery(id+"F3.wireOp",EDGE,"E93.MirrorCS"),sQuery(id+"F3.wireOp",EDGE,"E97.MirrorCS"),sQuery(id+"F3.wireOp",EDGE,"E99.MirrorCS"),sQuery(id+"F3.wireOp",EDGE,"E101.MirrorCS"),sQuery(id+"F3.wireOp",EDGE,"E103.MirrorCS"),sQuery(id+"F3.wireOp",EDGE,"E104.MirrorCS"),sQuery(id+"F3.wireOp",EDGE,"E105.MirrorCS"),sQuery(id+"F3.wireOp",EDGE,"E106"),sQuery(id+"F3.wireOp",EDGE,"E107"),sQuery(id+"F3.wireOp",EDGE,"E109.filletArc"),sQuery(id+"F3.wireOp",EDGE,"E110.0"),sQuery(id+"F3.wireOp",EDGE,"E111.0"),sQuery(id+"F3.wireOp",EDGE,"E112"),sQuery(id+"F3.wireOp",EDGE,"E113")])]});
            var Q3;
            Q3=makeQuery(id+"F7.opExtrude","SWEPT_BODY",BODY,{"disambiguationData":[OSD([sQuery(id+"F3.wireOp",EDGE,"E42")])]});
            var Q4;
            Q4=makeQuery(id+"F7.opExtrude","SWEPT_BODY",BODY,{"disambiguationData":[OSD([sQuery(id+"F3.wireOp",EDGE,"E90.MirrorCS")])]});
            var Q5;
            Q5=makeQuery(id+"F10.opExtrude","SWEPT_BODY",BODY,{"disambiguationData":[OSD([sQuery(id+"F3.wireOp",EDGE,"E13"),sQuery(id+"F3.wireOp",EDGE,"E17"),sQuery(id+"F3.wireOp",EDGE,"E44"),sQuery(id+"F3.wireOp",EDGE,"E79.MirrorCS")])]});
            transform(context, id + "F17", {"entities" : qUnion([Q0, Q1, Q2, Q3, Q4, Q5]), "transformType" : TransformType.TRANSLATION_3D, "dx" : 0 * mm, "dy" : 0 * mm, "dz" : -31.75 * mm, "makeCopy" : false});
        }
        {
            var Q0;
            Q0=makeQuery(id+"F7.opExtrude","SWEPT_FACE",FACE,{"disambiguationData":[OSD([sQuery(id+"F3.wireOp",EDGE,"E90.MirrorCS"),sQuery(id+"F3.wireOp",EDGE,"E99.MirrorCS")])]});
            var sketch = newSketch(context, id + "F18", { "sketchPlane" : qUnion([Q0])});
            skArc(sketch, "E143.0", {"start": v(479.76, 160.21) * mm, "mid": v(422, 136.55) * mm, "end": v(374.86, 95.65) * mm});
            skLineSegment(sketch, "E144.0", {"start": v(479.76, 254) * mm, "end": v(328.55, 254) * mm});
            skLineSegment(sketch, "E145.0", {"start": v(374.86, 95.65) * mm, "end": v(374.86, 149.41) * mm});
            skLineSegment(sketch, "E146.0", {"start": v(479.76, 146.05) * mm, "end": v(479.76, 199.13) * mm});
            skArc(sketch, "E147.0", {"start": v(479.76, 199.13) * mm, "mid": v(424.13, 180.99) * mm, "end": v(374.86, 149.41) * mm});
            skArc(sketch, "E148.0", {"start": v(479.76, 218.5) * mm, "mid": v(424.71, 202.14) * mm, "end": v(374.86, 173.63) * mm});
            skLineSegment(sketch, "E149.trimOffspring", {"start": v(374.86, 173.63) * mm, "end": v(374.86, 273.05) * mm});
            skLineSegment(sketch, "E150.trimOffspring", {"start": v(479.76, 218.5) * mm, "end": v(479.76, 273.05) * mm});
            skSolve(sketch);
        }
        {
            var Q0;
            Q0 = qSketchRegion(id + "F18", true);
            extrude(context, id + "F19", {"entities" : qUnion([Q0]), "operationType" : NewBodyOperationType.REMOVE, "oppositeDirection" : true, "depth" : 101.6 * mm, "offsetDistance" : 25.4 * mm});
        }
        {
            var Q0;
            Q0=makeQuery(id+"F4.opExtrude","SWEPT_FACE",FACE,{"disambiguationData":[OSD([sQuery(id+"F3.wireOp",EDGE,"E97.MirrorCS")])]});
            var sketch = newSketch(context, id + "F20", { "sketchPlane" : qUnion([Q0])});
            skLineSegment(sketch, "E151", {"start": v(320.08, 273.05) * mm, "end": v(345.48, 273.05) * mm});
            skLineSegment(sketch, "E152", {"start": v(345.48, 273.05) * mm, "end": v(345.48, 19.05) * mm});
            skLineSegment(sketch, "E153", {"start": v(345.48, 146.05) * mm, "end": v(335.48, 146.05) * mm});
            skLineSegment(sketch, "E154", {"start": v(345.48, 146.05) * mm, "end": v(345.48, 184.15) * mm});
            skLineSegment(sketch, "E155", {"start": v(345.48, 184.15) * mm, "end": v(345.48, 222.25) * mm});
            skLineSegment(sketch, "E156", {"start": v(345.48, 222.25) * mm, "end": v(345.48, 260.35) * mm});
            skLineSegment(sketch, "E157.MirrorCS", {"start": v(345.48, 146.05) * mm, "end": v(345.48, 107.95) * mm});
            skLineSegment(sketch, "E158.MirrorCS", {"start": v(345.48, 107.95) * mm, "end": v(345.48, 69.85) * mm});
            skLineSegment(sketch, "E159.MirrorCS", {"start": v(345.48, 69.85) * mm, "end": v(345.48, 31.75) * mm});
            skSolve(sketch);
        }
        {
            var Q0;
            Q0=sQuery(id+"F20.wireOp",VERTEX,"E159.MirrorCS.end");
            var Q1;
            Q1=sQuery(id+"F20.wireOp",VERTEX,"E158.MirrorCS.end");
            var Q2;
            Q2=sQuery(id+"F20.wireOp",VERTEX,"E158.MirrorCS.start");
            var Q3;
            Q3=sQuery(id+"F20.wireOp",VERTEX,"E157.MirrorCS.start");
            var Q4;
            Q4=sQuery(id+"F20.wireOp",VERTEX,"E155.start");
            var Q5;
            Q5=sQuery(id+"F20.wireOp",VERTEX,"E156.start");
            var Q6;
            Q6=sQuery(id+"F20.wireOp",VERTEX,"E156.end");
            var Q7;
            Q7=makeQuery(id+"F7.opExtrude","SWEPT_BODY",BODY,{"disambiguationData":[OSD([sQuery(id+"F3.wireOp",EDGE,"E42")])]});
            var Q8;
            Q8=makeQuery(id+"F7.opExtrude","SWEPT_BODY",BODY,{"disambiguationData":[OSD([sQuery(id+"F3.wireOp",EDGE,"E90.MirrorCS")])]});
            var Q9;
            Q9=makeQuery(id+"F4.opExtrude","SWEPT_BODY",BODY,{"disambiguationData":[OSD([sQuery(id+"F3.wireOp",EDGE,"E24"),sQuery(id+"F3.wireOp",EDGE,"E26"),sQuery(id+"F3.wireOp",EDGE,"E27"),sQuery(id+"F3.wireOp",EDGE,"E37"),sQuery(id+"F3.wireOp",EDGE,"E38.trimOffspring"),sQuery(id+"F3.wireOp",EDGE,"E39.trimOffspring"),sQuery(id+"F3.wireOp",EDGE,"E40"),sQuery(id+"F3.wireOp",EDGE,"E41"),sQuery(id+"F3.wireOp",EDGE,"E42"),sQuery(id+"F3.wireOp",EDGE,"E43.trimOffspring"),sQuery(id+"F3.wireOp",EDGE,"E49.filletArc"),sQuery(id+"F3.wireOp",EDGE,"E50.filletArc"),sQuery(id+"F3.wireOp",EDGE,"E51.filletArc"),sQuery(id+"F3.wireOp",EDGE,"E52.filletArc"),sQuery(id+"F3.wireOp",EDGE,"E53.trimOffspring"),sQuery(id+"F3.wireOp",EDGE,"E54.trimOffspring"),sQuery(id+"F3.wireOp",EDGE,"E57.filletArc"),sQuery(id+"F3.wireOp",EDGE,"E58.filletArc"),sQuery(id+"F3.wireOp",EDGE,"E81.MirrorCS"),sQuery(id+"F3.wireOp",EDGE,"E82.MirrorCS"),sQuery(id+"F3.wireOp",EDGE,"E83.MirrorCS"),sQuery(id+"F3.wireOp",EDGE,"E84.MirrorCS"),sQuery(id+"F3.wireOp",EDGE,"E85.MirrorCS"),sQuery(id+"F3.wireOp",EDGE,"E86.MirrorCS"),sQuery(id+"F3.wireOp",EDGE,"E87.MirrorCS"),sQuery(id+"F3.wireOp",EDGE,"E88.MirrorCS"),sQuery(id+"F3.wireOp",EDGE,"E89.MirrorCS"),sQuery(id+"F3.wireOp",EDGE,"E90.MirrorCS"),sQuery(id+"F3.wireOp",EDGE,"E91.MirrorCS"),sQuery(id+"F3.wireOp",EDGE,"E93.MirrorCS"),sQuery(id+"F3.wireOp",EDGE,"E97.MirrorCS"),sQuery(id+"F3.wireOp",EDGE,"E99.MirrorCS"),sQuery(id+"F3.wireOp",EDGE,"E101.MirrorCS"),sQuery(id+"F3.wireOp",EDGE,"E103.MirrorCS"),sQuery(id+"F3.wireOp",EDGE,"E104.MirrorCS"),sQuery(id+"F3.wireOp",EDGE,"E105.MirrorCS"),sQuery(id+"F3.wireOp",EDGE,"E106"),sQuery(id+"F3.wireOp",EDGE,"E107"),sQuery(id+"F3.wireOp",EDGE,"E109.filletArc"),sQuery(id+"F3.wireOp",EDGE,"E110.0"),sQuery(id+"F3.wireOp",EDGE,"E111.0"),sQuery(id+"F3.wireOp",EDGE,"E112"),sQuery(id+"F3.wireOp",EDGE,"E113")])]});
            hole(context, id + "F21", {"style" : HoleStyle.SIMPLE, "endStyle" : HoleEndStyle.BLIND, "standardTappedOrClearance" : lookupTablePath({ "standard" : "ANSI", "fit" : "Close", "size" : "#8", "type" : "Clearance" }), "standardBlindInLast" : lookupTablePath({ "fit" : "Close", "standard" : "ANSI", "size" : "#8", "type" : "Clearance" }), "holeDiameter" : 4.32 * mm, "holeDepth" : 76.2 * mm, "isTappedThrough" : true, "tappedDepth" : 12.7 * mm, "tapClearance" : 3, "locations" : qUnion([Q0, Q1, Q2, Q3, Q4, Q5, Q6]), "scope" : qUnion([Q7, Q8, Q9])});
        }
        {
            var Q0;
            Q0=makeQuery(id+"F4.opExtrude","SWEPT_FACE",FACE,{"disambiguationData":[OSD([sQuery(id+"F3.wireOp",EDGE,"E78.MirrorCS")])]});
            var sketch = newSketch(context, id + "F22", { "sketchPlane" : qUnion([Q0])});
            skLineSegment(sketch, "E160", {"start": v(511.68, 273.05) * mm, "end": v(511.68, 146.05) * mm});
            skLineSegment(sketch, "E161", {"start": v(511.68, 209.55) * mm, "end": v(517.7, 209.55) * mm});
            skPoint(sketch, "E161.endSnap0", {"position": v(511.68, 209.55) * mm});
            skLineSegment(sketch, "E162", {"start": v(511.68, 209.55) * mm, "end": v(511.68, 234.95) * mm});
            skLineSegment(sketch, "E163", {"start": v(511.68, 234.95) * mm, "end": v(511.68, 260.35) * mm});
            skLineSegment(sketch, "E164.MirrorCS", {"start": v(511.68, 209.55) * mm, "end": v(511.68, 184.15) * mm});
            skLineSegment(sketch, "E165.MirrorCS", {"start": v(511.68, 184.15) * mm, "end": v(511.68, 158.75) * mm});
            skSolve(sketch);
        }
        {
            var Q0;
            Q0=sQuery(id+"F22.wireOp",VERTEX,"E163.end");
            var Q1;
            Q1=sQuery(id+"F22.wireOp",VERTEX,"E163.start");
            var Q2;
            Q2=sQuery(id+"F22.wireOp",VERTEX,"E161.endSnap0");
            var Q3;
            Q3=sQuery(id+"F22.wireOp",VERTEX,"E164.MirrorCS.end");
            var Q4;
            Q4=sQuery(id+"F22.wireOp",VERTEX,"E165.MirrorCS.end");
            var Q5;
            Q5=makeQuery(id+"F4.opExtrude","SWEPT_BODY",BODY,{"disambiguationData":[OSD([sQuery(id+"F3.wireOp",EDGE,"E14"),sQuery(id+"F3.wireOp",EDGE,"E17"),sQuery(id+"F3.wireOp",EDGE,"E20"),sQuery(id+"F3.wireOp",EDGE,"E22"),sQuery(id+"F3.wireOp",EDGE,"E31"),sQuery(id+"F3.wireOp",EDGE,"E32"),sQuery(id+"F3.wireOp",EDGE,"E33"),sQuery(id+"F3.wireOp",EDGE,"E34.trimOffspring"),sQuery(id+"F3.wireOp",EDGE,"E35.trimOffspring"),sQuery(id+"F3.wireOp",EDGE,"E44"),sQuery(id+"F3.wireOp",EDGE,"E45.filletArc"),sQuery(id+"F3.wireOp",EDGE,"E46.filletArc"),sQuery(id+"F3.wireOp",EDGE,"E47.filletArc"),sQuery(id+"F3.wireOp",EDGE,"E48.filletArc"),sQuery(id+"F3.wireOp",EDGE,"E55.filletArc"),sQuery(id+"F3.wireOp",EDGE,"E56.filletArc"),sQuery(id+"F3.wireOp",EDGE,"E59.MirrorCS"),sQuery(id+"F3.wireOp",EDGE,"E60.MirrorCS"),sQuery(id+"F3.wireOp",EDGE,"E61.MirrorCS"),sQuery(id+"F3.wireOp",EDGE,"E62.MirrorCS"),sQuery(id+"F3.wireOp",EDGE,"E63.MirrorCS"),sQuery(id+"F3.wireOp",EDGE,"E64.MirrorCS"),sQuery(id+"F3.wireOp",EDGE,"E65.MirrorCS"),sQuery(id+"F3.wireOp",EDGE,"E66.MirrorCS"),sQuery(id+"F3.wireOp",EDGE,"E75.MirrorCS"),sQuery(id+"F3.wireOp",EDGE,"E76.MirrorCS"),sQuery(id+"F3.wireOp",EDGE,"E77.MirrorCS"),sQuery(id+"F3.wireOp",EDGE,"E78.MirrorCS"),sQuery(id+"F3.wireOp",EDGE,"E79.MirrorCS"),sQuery(id+"F3.wireOp",EDGE,"E114.trimOffspring"),sQuery(id+"F3.wireOp",EDGE,"E115.trimOffspring"),sQuery(id+"F3.wireOp",EDGE,"E116.trimOffspring"),sQuery(id+"F3.wireOp",EDGE,"E117.filletArc"),sQuery(id+"F3.wireOp",EDGE,"E118.filletArc")])]});
            var Q6;
            Q6=makeQuery(id+"F7.opExtrude","SWEPT_BODY",BODY,{"disambiguationData":[OSD([sQuery(id+"F3.wireOp",EDGE,"E42")])]});
            var Q7;
            Q7=makeQuery(id+"F7.opExtrude","SWEPT_BODY",BODY,{"disambiguationData":[OSD([sQuery(id+"F3.wireOp",EDGE,"E90.MirrorCS")])]});
            hole(context, id + "F23", {"style" : HoleStyle.SIMPLE, "endStyle" : HoleEndStyle.BLIND, "standardTappedOrClearance" : lookupTablePath({ "standard" : "ANSI", "fit" : "Close", "size" : "#8", "type" : "Clearance" }), "standardBlindInLast" : lookupTablePath({ "fit" : "Close", "standard" : "ANSI", "size" : "#8", "type" : "Clearance" }), "holeDiameter" : 4.32 * mm, "holeDepth" : 76.2 * mm, "isTappedThrough" : true, "tappedDepth" : 12.7 * mm, "tapClearance" : 3, "locations" : qUnion([Q0, Q1, Q2, Q3, Q4]), "scope" : qUnion([Q5, Q6, Q7])});
        }
        {
            var Q0;
            Q0=makeQuery(id+"F4.opExtrude","SWEPT_FACE",FACE,{"disambiguationData":[OSD([sQuery(id+"F3.wireOp",EDGE,"E103.MirrorCS")])]});
            var sketch = newSketch(context, id + "F24", { "sketchPlane" : qUnion([Q0])});
            skLineSegment(sketch, "E166", {"start": v(196.17, 273.05) * mm, "end": v(196.17, 146.05) * mm});
            skLineSegment(sketch, "E167", {"start": v(196.17, 146.05) * mm, "end": v(196.17, 184.15) * mm});
            skLineSegment(sketch, "E168", {"start": v(196.17, 184.15) * mm, "end": v(196.17, 222.25) * mm});
            skLineSegment(sketch, "E169", {"start": v(196.17, 222.25) * mm, "end": v(196.17, 260.35) * mm});
            skLineSegment(sketch, "E170", {"start": v(196.17, 146.05) * mm, "end": v(135.22, 146.05) * mm});
            skLineSegment(sketch, "E171.MirrorCS", {"start": v(196.17, 19.05) * mm, "end": v(196.17, 146.05) * mm});
            skLineSegment(sketch, "E172.MirrorCS", {"start": v(196.17, 146.05) * mm, "end": v(196.17, 107.95) * mm});
            skLineSegment(sketch, "E173.MirrorCS", {"start": v(196.17, 107.95) * mm, "end": v(196.17, 69.85) * mm});
            skLineSegment(sketch, "E174.MirrorCS", {"start": v(196.17, 69.85) * mm, "end": v(196.17, 31.75) * mm});
            skSolve(sketch);
        }
        {
            var Q0;
            Q0=makeQuery(id+"F4.opExtrude","SWEPT_FACE",FACE,{"disambiguationData":[OSD([sQuery(id+"F3.wireOp",EDGE,"E40")])]});
            var sketch = newSketch(context, id + "F25", { "sketchPlane" : qUnion([Q0])});
            skLineSegment(sketch, "E175", {"start": v(-196.17, 273.05) * mm, "end": v(-196.17, 146.05) * mm});
            skLineSegment(sketch, "E176", {"start": v(-196.17, 146.05) * mm, "end": v(-152.27, 146.05) * mm});
            skLineSegment(sketch, "E177", {"start": v(-196.17, 146.05) * mm, "end": v(-196.17, 184.15) * mm});
            skLineSegment(sketch, "E178", {"start": v(-196.17, 184.15) * mm, "end": v(-196.17, 222.25) * mm});
            skLineSegment(sketch, "E179", {"start": v(-196.17, 222.25) * mm, "end": v(-196.17, 260.35) * mm});
            skLineSegment(sketch, "E180.MirrorCS", {"start": v(-196.17, 146.05) * mm, "end": v(-196.17, 107.95) * mm});
            skLineSegment(sketch, "E181.MirrorCS", {"start": v(-196.17, 69.85) * mm, "end": v(-196.17, 31.75) * mm});
            skLineSegment(sketch, "E182.MirrorCS", {"start": v(-196.17, 107.95) * mm, "end": v(-196.17, 69.85) * mm});
            skLineSegment(sketch, "E183.MirrorCS", {"start": v(-196.17, 19.05) * mm, "end": v(-196.17, 146.05) * mm});
            skSolve(sketch);
        }
        {
            var Q0;
            Q0=sQuery(id+"F25.wireOp",VERTEX,"E179.end");
            var Q1;
            Q1=sQuery(id+"F25.wireOp",VERTEX,"E178.end");
            var Q2;
            Q2=sQuery(id+"F25.wireOp",VERTEX,"E177.end");
            var Q3;
            Q3=sQuery(id+"F25.wireOp",VERTEX,"E177.start");
            var Q4;
            Q4=sQuery(id+"F25.wireOp",VERTEX,"E182.MirrorCS.start");
            var Q5;
            Q5=sQuery(id+"F25.wireOp",VERTEX,"E182.MirrorCS.end");
            var Q6;
            Q6=sQuery(id+"F25.wireOp",VERTEX,"E181.MirrorCS.end");
            var Q7;
            Q7=makeQuery(id+"F4.opExtrude","SWEPT_BODY",BODY,{"disambiguationData":[OSD([sQuery(id+"F3.wireOp",EDGE,"E24"),sQuery(id+"F3.wireOp",EDGE,"E26"),sQuery(id+"F3.wireOp",EDGE,"E27"),sQuery(id+"F3.wireOp",EDGE,"E37"),sQuery(id+"F3.wireOp",EDGE,"E38.trimOffspring"),sQuery(id+"F3.wireOp",EDGE,"E39.trimOffspring"),sQuery(id+"F3.wireOp",EDGE,"E40"),sQuery(id+"F3.wireOp",EDGE,"E41"),sQuery(id+"F3.wireOp",EDGE,"E42"),sQuery(id+"F3.wireOp",EDGE,"E43.trimOffspring"),sQuery(id+"F3.wireOp",EDGE,"E49.filletArc"),sQuery(id+"F3.wireOp",EDGE,"E50.filletArc"),sQuery(id+"F3.wireOp",EDGE,"E51.filletArc"),sQuery(id+"F3.wireOp",EDGE,"E52.filletArc"),sQuery(id+"F3.wireOp",EDGE,"E53.trimOffspring"),sQuery(id+"F3.wireOp",EDGE,"E54.trimOffspring"),sQuery(id+"F3.wireOp",EDGE,"E57.filletArc"),sQuery(id+"F3.wireOp",EDGE,"E58.filletArc"),sQuery(id+"F3.wireOp",EDGE,"E81.MirrorCS"),sQuery(id+"F3.wireOp",EDGE,"E82.MirrorCS"),sQuery(id+"F3.wireOp",EDGE,"E83.MirrorCS"),sQuery(id+"F3.wireOp",EDGE,"E84.MirrorCS"),sQuery(id+"F3.wireOp",EDGE,"E85.MirrorCS"),sQuery(id+"F3.wireOp",EDGE,"E86.MirrorCS"),sQuery(id+"F3.wireOp",EDGE,"E87.MirrorCS"),sQuery(id+"F3.wireOp",EDGE,"E88.MirrorCS"),sQuery(id+"F3.wireOp",EDGE,"E89.MirrorCS"),sQuery(id+"F3.wireOp",EDGE,"E90.MirrorCS"),sQuery(id+"F3.wireOp",EDGE,"E91.MirrorCS"),sQuery(id+"F3.wireOp",EDGE,"E93.MirrorCS"),sQuery(id+"F3.wireOp",EDGE,"E97.MirrorCS"),sQuery(id+"F3.wireOp",EDGE,"E99.MirrorCS"),sQuery(id+"F3.wireOp",EDGE,"E101.MirrorCS"),sQuery(id+"F3.wireOp",EDGE,"E103.MirrorCS"),sQuery(id+"F3.wireOp",EDGE,"E104.MirrorCS"),sQuery(id+"F3.wireOp",EDGE,"E105.MirrorCS"),sQuery(id+"F3.wireOp",EDGE,"E106"),sQuery(id+"F3.wireOp",EDGE,"E107"),sQuery(id+"F3.wireOp",EDGE,"E109.filletArc"),sQuery(id+"F3.wireOp",EDGE,"E110.0"),sQuery(id+"F3.wireOp",EDGE,"E111.0"),sQuery(id+"F3.wireOp",EDGE,"E112"),sQuery(id+"F3.wireOp",EDGE,"E113")])]});
            var Q8;
            Q8=makeQuery(id+"F2.opExtrude","SWEPT_BODY",BODY,{"disambiguationData":[OSD([sQuery(id+"F0.wireOp",EDGE,"E0.bottom"),sQuery(id+"F0.wireOp",EDGE,"E0.top"),sQuery(id+"F0.wireOp",EDGE,"E0.left"),sQuery(id+"F0.wireOp",EDGE,"E0.right"),sQuery(id+"F0.wireOp",EDGE,"E7"),sQuery(id+"F0.wireOp",EDGE,"E8"),sQuery(id+"F0.wireOp",EDGE,"E9"),sQuery(id+"F0.wireOp",EDGE,"E10"),sQuery(id+"F0.wireOp",EDGE,"E11.1.0"),sQuery(id+"F0.wireOp",EDGE,"E11.1.1"),sQuery(id+"F0.wireOp",EDGE,"E11.1.2"),sQuery(id+"F0.wireOp",EDGE,"E11.1.3"),sQuery(id+"F0.wireOp",EDGE,"E11.1.4"),sQuery(id+"F0.wireOp",EDGE,"E11.2.0"),sQuery(id+"F0.wireOp",EDGE,"E11.2.1"),sQuery(id+"F0.wireOp",EDGE,"E11.2.2"),sQuery(id+"F0.wireOp",EDGE,"E11.2.3"),sQuery(id+"F0.wireOp",EDGE,"E11.2.4"),sQuery(id+"F0.wireOp",EDGE,"E11.3.0"),sQuery(id+"F0.wireOp",EDGE,"E11.3.1"),sQuery(id+"F0.wireOp",EDGE,"E11.3.2"),sQuery(id+"F0.wireOp",EDGE,"E11.3.3"),sQuery(id+"F0.wireOp",EDGE,"E11.3.4"),sQuery(id+"F0.wireOp",EDGE,"E12.0"),sQuery(id+"F0.wireOp",EDGE,"E12.1"),sQuery(id+"F0.wireOp",EDGE,"E12.2"),sQuery(id+"F0.wireOp",EDGE,"E12.3")])]});
            hole(context, id + "F26", {"style" : HoleStyle.SIMPLE, "endStyle" : HoleEndStyle.BLIND, "standardTappedOrClearance" : lookupTablePath({ "standard" : "ANSI", "fit" : "Close", "size" : "#8", "type" : "Clearance" }), "standardBlindInLast" : lookupTablePath({ "fit" : "Close", "standard" : "ANSI", "size" : "#8", "type" : "Clearance" }), "holeDiameter" : 4.32 * mm, "holeDepth" : 76.2 * mm, "isTappedThrough" : true, "tappedDepth" : 12.7 * mm, "tapClearance" : 3, "locations" : qUnion([Q0, Q1, Q2, Q3, Q4, Q5, Q6]), "scope" : qUnion([Q7, Q8])});
        }
        {
            var Q0;
            Q0=sQuery(id+"F24.wireOp",VERTEX,"E169.end");
            var Q1;
            Q1=sQuery(id+"F24.wireOp",VERTEX,"E169.start");
            var Q2;
            Q2=sQuery(id+"F24.wireOp",VERTEX,"E168.start");
            var Q3;
            Q3=sQuery(id+"F24.wireOp",VERTEX,"E166.end");
            var Q4;
            Q4=sQuery(id+"F24.wireOp",VERTEX,"E172.MirrorCS.end");
            var Q5;
            Q5=sQuery(id+"F24.wireOp",VERTEX,"E173.MirrorCS.end");
            var Q6;
            Q6=sQuery(id+"F24.wireOp",VERTEX,"E174.MirrorCS.end");
            var Q7;
            Q7=makeQuery(id+"F4.opExtrude","SWEPT_BODY",BODY,{"disambiguationData":[OSD([sQuery(id+"F3.wireOp",EDGE,"E24"),sQuery(id+"F3.wireOp",EDGE,"E26"),sQuery(id+"F3.wireOp",EDGE,"E27"),sQuery(id+"F3.wireOp",EDGE,"E37"),sQuery(id+"F3.wireOp",EDGE,"E38.trimOffspring"),sQuery(id+"F3.wireOp",EDGE,"E39.trimOffspring"),sQuery(id+"F3.wireOp",EDGE,"E40"),sQuery(id+"F3.wireOp",EDGE,"E41"),sQuery(id+"F3.wireOp",EDGE,"E42"),sQuery(id+"F3.wireOp",EDGE,"E43.trimOffspring"),sQuery(id+"F3.wireOp",EDGE,"E49.filletArc"),sQuery(id+"F3.wireOp",EDGE,"E50.filletArc"),sQuery(id+"F3.wireOp",EDGE,"E51.filletArc"),sQuery(id+"F3.wireOp",EDGE,"E52.filletArc"),sQuery(id+"F3.wireOp",EDGE,"E53.trimOffspring"),sQuery(id+"F3.wireOp",EDGE,"E54.trimOffspring"),sQuery(id+"F3.wireOp",EDGE,"E57.filletArc"),sQuery(id+"F3.wireOp",EDGE,"E58.filletArc"),sQuery(id+"F3.wireOp",EDGE,"E81.MirrorCS"),sQuery(id+"F3.wireOp",EDGE,"E82.MirrorCS"),sQuery(id+"F3.wireOp",EDGE,"E83.MirrorCS"),sQuery(id+"F3.wireOp",EDGE,"E84.MirrorCS"),sQuery(id+"F3.wireOp",EDGE,"E85.MirrorCS"),sQuery(id+"F3.wireOp",EDGE,"E86.MirrorCS"),sQuery(id+"F3.wireOp",EDGE,"E87.MirrorCS"),sQuery(id+"F3.wireOp",EDGE,"E88.MirrorCS"),sQuery(id+"F3.wireOp",EDGE,"E89.MirrorCS"),sQuery(id+"F3.wireOp",EDGE,"E90.MirrorCS"),sQuery(id+"F3.wireOp",EDGE,"E91.MirrorCS"),sQuery(id+"F3.wireOp",EDGE,"E93.MirrorCS"),sQuery(id+"F3.wireOp",EDGE,"E97.MirrorCS"),sQuery(id+"F3.wireOp",EDGE,"E99.MirrorCS"),sQuery(id+"F3.wireOp",EDGE,"E101.MirrorCS"),sQuery(id+"F3.wireOp",EDGE,"E103.MirrorCS"),sQuery(id+"F3.wireOp",EDGE,"E104.MirrorCS"),sQuery(id+"F3.wireOp",EDGE,"E105.MirrorCS"),sQuery(id+"F3.wireOp",EDGE,"E106"),sQuery(id+"F3.wireOp",EDGE,"E107"),sQuery(id+"F3.wireOp",EDGE,"E109.filletArc"),sQuery(id+"F3.wireOp",EDGE,"E110.0"),sQuery(id+"F3.wireOp",EDGE,"E111.0"),sQuery(id+"F3.wireOp",EDGE,"E112"),sQuery(id+"F3.wireOp",EDGE,"E113")])]});
            var Q8;
            Q8=makeQuery(id+"F2.opExtrude","SWEPT_BODY",BODY,{"disambiguationData":[OSD([sQuery(id+"F0.wireOp",EDGE,"E0.bottom"),sQuery(id+"F0.wireOp",EDGE,"E0.top"),sQuery(id+"F0.wireOp",EDGE,"E0.left"),sQuery(id+"F0.wireOp",EDGE,"E0.right"),sQuery(id+"F0.wireOp",EDGE,"E7"),sQuery(id+"F0.wireOp",EDGE,"E8"),sQuery(id+"F0.wireOp",EDGE,"E9"),sQuery(id+"F0.wireOp",EDGE,"E10"),sQuery(id+"F0.wireOp",EDGE,"E11.1.0"),sQuery(id+"F0.wireOp",EDGE,"E11.1.1"),sQuery(id+"F0.wireOp",EDGE,"E11.1.2"),sQuery(id+"F0.wireOp",EDGE,"E11.1.3"),sQuery(id+"F0.wireOp",EDGE,"E11.1.4"),sQuery(id+"F0.wireOp",EDGE,"E11.2.0"),sQuery(id+"F0.wireOp",EDGE,"E11.2.1"),sQuery(id+"F0.wireOp",EDGE,"E11.2.2"),sQuery(id+"F0.wireOp",EDGE,"E11.2.3"),sQuery(id+"F0.wireOp",EDGE,"E11.2.4"),sQuery(id+"F0.wireOp",EDGE,"E11.3.0"),sQuery(id+"F0.wireOp",EDGE,"E11.3.1"),sQuery(id+"F0.wireOp",EDGE,"E11.3.2"),sQuery(id+"F0.wireOp",EDGE,"E11.3.3"),sQuery(id+"F0.wireOp",EDGE,"E11.3.4"),sQuery(id+"F0.wireOp",EDGE,"E12.0"),sQuery(id+"F0.wireOp",EDGE,"E12.1"),sQuery(id+"F0.wireOp",EDGE,"E12.2"),sQuery(id+"F0.wireOp",EDGE,"E12.3")])]});
            hole(context, id + "F27", {"style" : HoleStyle.SIMPLE, "endStyle" : HoleEndStyle.BLIND, "standardTappedOrClearance" : lookupTablePath({ "standard" : "ANSI", "fit" : "Close", "size" : "#8", "type" : "Clearance" }), "standardBlindInLast" : lookupTablePath({ "fit" : "Close", "standard" : "ANSI", "size" : "#8", "type" : "Clearance" }), "holeDiameter" : 4.32 * mm, "holeDepth" : 76.2 * mm, "isTappedThrough" : true, "tappedDepth" : 12.7 * mm, "tapClearance" : 3, "locations" : qUnion([Q0, Q1, Q2, Q3, Q4, Q5, Q6]), "scope" : qUnion([Q7, Q8])});
        }
    });
